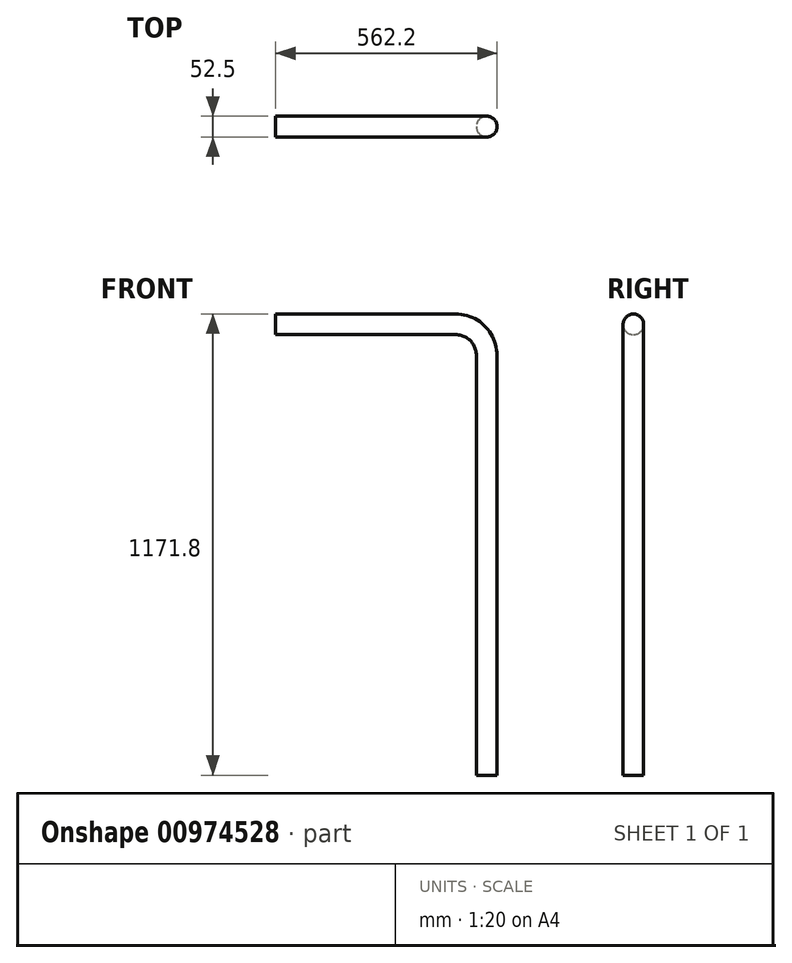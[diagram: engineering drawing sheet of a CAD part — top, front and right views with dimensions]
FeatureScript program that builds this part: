
annotation { "Feature Type Name" : "Feature", "Feature Type Description" : "" }
export const myFeature = defineFeature(function(context is Context, id is Id, definition is map)
    precondition{}
    {
        {
            var Q0;
            Q0=qCreatedBy(makeId("Right.planeOp"),FACE);
            var sketch = newSketch(context, id + "F0", { "sketchPlane" : qUnion([Q0])});
            skCircle(sketch, "E0", {"center": v(0, 0) * mm, "radius": 26.25 * mm});
            skSolve(sketch);
        }
        {
            var Q0;
            Q0=qCreatedBy(makeId("Front.planeOp"),FACE);
            var sketch = newSketch(context, id + "F1", { "sketchPlane" : qUnion([Q0])});
            skArc(sketch, "E1", {"start": v(0, 0) * mm, "mid": v(55.69, -23.07) * mm, "end": v(78.75, -78.75) * mm});
            skLineSegment(sketch, "E2.0", {"start": v(0, 26.25) * mm, "end": v(0, -26.25) * mm, "construction": true});
            skSolve(sketch);
        }
        {
            var Q0;
            Q0=makeQuery(id+"F0.imprint","IMPRINT",FACE,{"disambiguationData":[TD([[makeQuery(id+"F0.imprint","IMPRINT",EDGE,{"derivedFrom":sQuery(id+"F0.wireOp",EDGE,"E0")}),1.0]])]});
            var Q1;
            Q1=qConstructionFilter(qBodyType(qCreatedBy(id+"F1",EDGE),BodyType.WIRE),ConstructionObject.NO);
            sweep(context, id + "F2", {"profiles" : qUnion([Q0]), "path" : qUnion([Q1])});
        }
        {
            var Q0;
            Q0=makeQuery(id+"F2.opSweep","CAP_FACE",FACE,{"disambiguationData":[OSD([sQuery(id+"F0.wireOp",EDGE,"E0"),sQuery(id+"F1.wireOp",VERTEX,"E1.end")])],"isStart":false});
            extrude(context, id + "F3", {"entities" : qUnion([Q0]), "operationType" : NewBodyOperationType.ADD, "depth" : 1066.8 * mm, "offsetDistance" : 25.4 * mm});
        }
        {
            var Q0;
            Q0=makeQuery(id+"F2.opSweep","CAP_FACE",FACE,{"disambiguationData":[OSD([sQuery(id+"F0.wireOp",EDGE,"E0"),sQuery(id+"F1.wireOp",VERTEX,"E1.start")])],"isStart":true});
            extrude(context, id + "F4", {"entities" : qUnion([Q0]), "operationType" : NewBodyOperationType.ADD, "depth" : 457.2 * mm, "offsetDistance" : 25.4 * mm});
        }
    });
